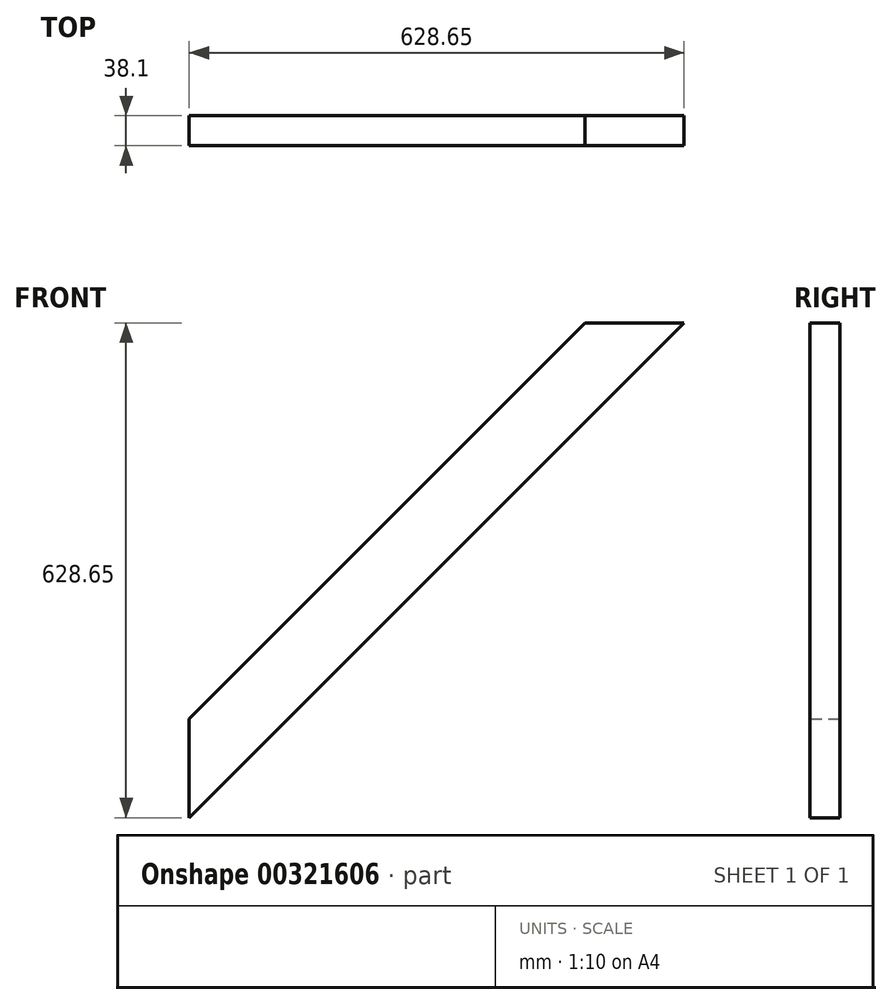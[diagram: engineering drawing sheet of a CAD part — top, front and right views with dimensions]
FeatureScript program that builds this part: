
annotation { "Feature Type Name" : "Feature", "Feature Type Description" : "" }
export const myFeature = defineFeature(function(context is Context, id is Id, definition is map)
    precondition{}
    {
        {
            var Q0;
            Q0=qCreatedBy(makeId("Front.planeOp"),FACE);
            var sketch = newSketch(context, id + "F0", { "sketchPlane" : qUnion([Q0])});
            skLineSegment(sketch, "E0", {"start": v(359.07, 357.2) * mm, "end": v(233.34, 357.2) * mm});
            skLineSegment(sketch, "E1", {"start": v(233.34, 357.2) * mm, "end": v(-269.58, -145.72) * mm});
            skLineSegment(sketch, "E2", {"start": v(-269.58, -145.72) * mm, "end": v(-269.58, -271.45) * mm});
            skLineSegment(sketch, "E3", {"start": v(-269.58, -271.45) * mm, "end": v(359.07, 357.2) * mm});
            skSolve(sketch);
        }
        {
            var Q0;
            Q0=makeQuery(id+"F0.imprint","IMPRINT",FACE,{"disambiguationData":[TD([[makeQuery(id+"F0.imprint","IMPRINT",EDGE,{"derivedFrom":sQuery(id+"F0.wireOp",EDGE,"E0")}),1.0]])]});
            extrude(context, id + "F1", {"entities" : qUnion([Q0]), "depth" : 38.1 * mm});
        }
    });
